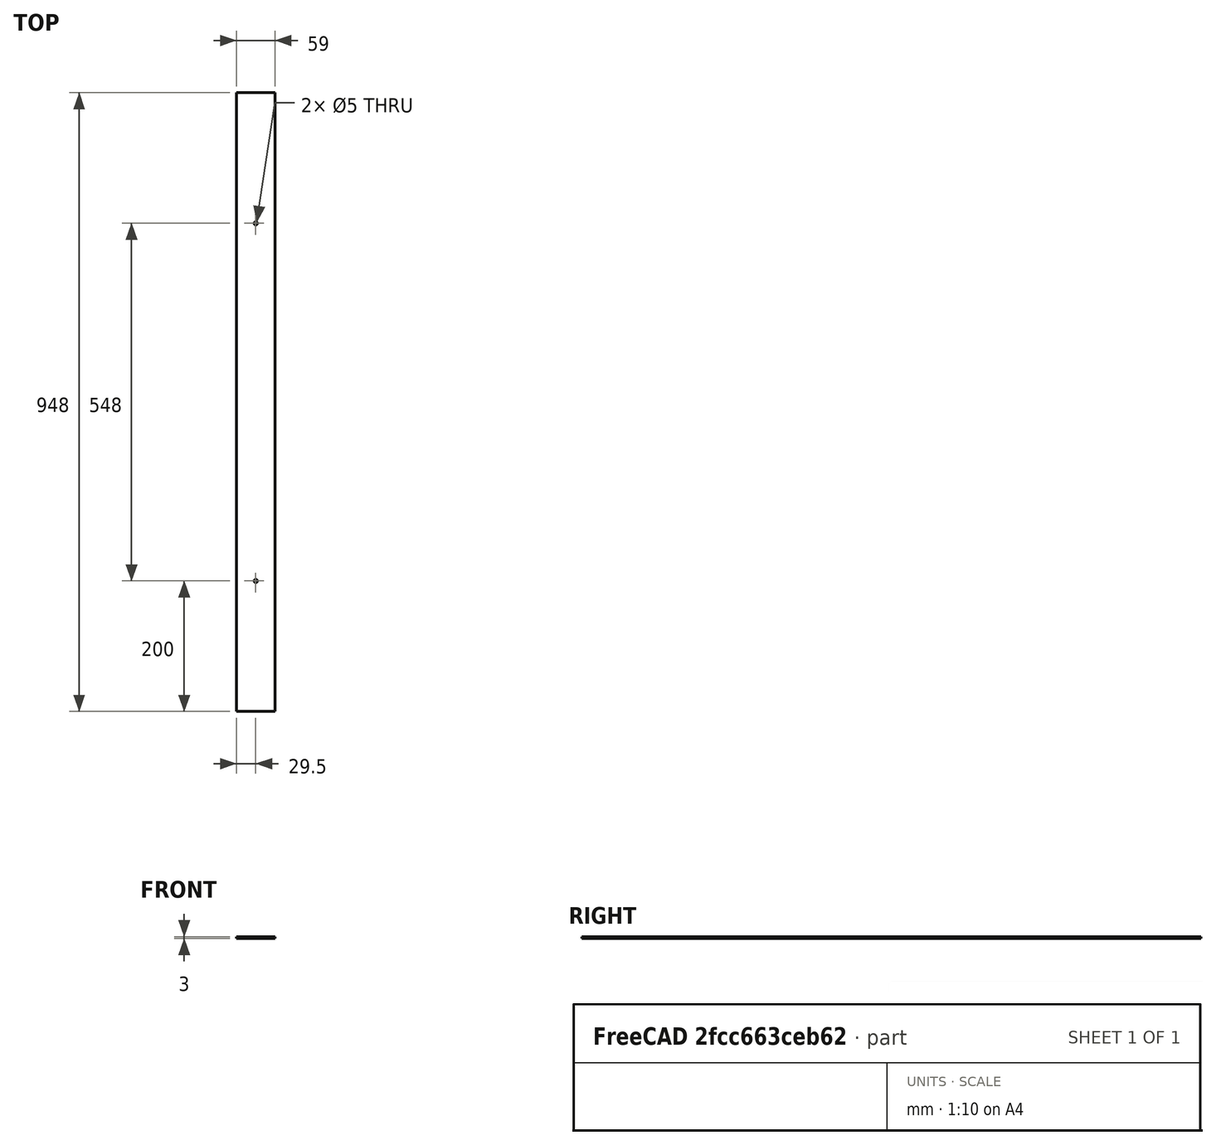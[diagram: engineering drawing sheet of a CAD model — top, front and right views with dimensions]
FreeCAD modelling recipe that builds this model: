
FCSTD DOCUMENT  (FreeCAD 0.16R6706 (Git))
Label: frame_cover_side
License: CreativeCommons Attribution-ShareAlike
LicenseURL: http://creativecommons.org/licenses/by-sa/4.0/
objects: Sketcher::SketchObject×1, PartDesign::Pad×1
note: 3 computed .brp shape members not serialized (recipe doc carries the construction recipe); baked Part::Feature solids carry a one-line shape summary decoded from their .brp

FEATURE [Sketcher::SketchObject] Sketch
  sketch-geometry (7):
    g0: LineSegment StartX=0 StartY=0 StartZ=0 EndX=59 EndY=0 EndZ=0
    g1: LineSegment StartX=59 StartY=0 StartZ=0 EndX=59 EndY=948 EndZ=0
    g2: LineSegment StartX=59 StartY=948 StartZ=0 EndX=0 EndY=948 EndZ=0
    g3: LineSegment StartX=0 StartY=948 StartZ=0 EndX=0 EndY=0 EndZ=0
    g4: LineSegment [constr] StartX=29.5 StartY=948 StartZ=0 EndX=29.5 EndY=0 EndZ=0
    g5: Circle CenterX=29.5 CenterY=200 CenterZ=0 NormalX=0 NormalY=0 NormalZ=1 Radius=2.5
    g6: Circle CenterX=29.5 CenterY=748 CenterZ=0 NormalX=0 NormalY=0 NormalZ=1 Radius=2.5
  constraints (21):
    c: Coincident(g0,g1)
    c: Coincident(g1,g2)
    c: Coincident(g2,g3)
    c: Coincident(g3,g0)
    c: Horizontal(g0)
    c: Horizontal(g2)
    c: Vertical(g1)
    c: Vertical(g3)
    c: Coincident(g0,g-1)
    c: DistanceX(g0,g0) = 59
    c: DistanceY(g1,g1) = 948
    c: PointOnObject(g4,g2)
    c: Vertical(g4)
    c: PointOnObject(g4,g0)
    c: Symmetric(g0,g-1,g4)
    c: PointOnObject(g5,g4)
    c: PointOnObject(g6,g4)
    c: DistanceY(g6,g1) = 200
    c: Radius(g6) = 2.5
    c: Equal(g6,g5)
    c: DistanceY(g0,g5) = 200
FEATURE [PartDesign::Pad] Pad
  Length = 3
  Length2 = 100
  Sketch = -> Sketch
  Type = 0
